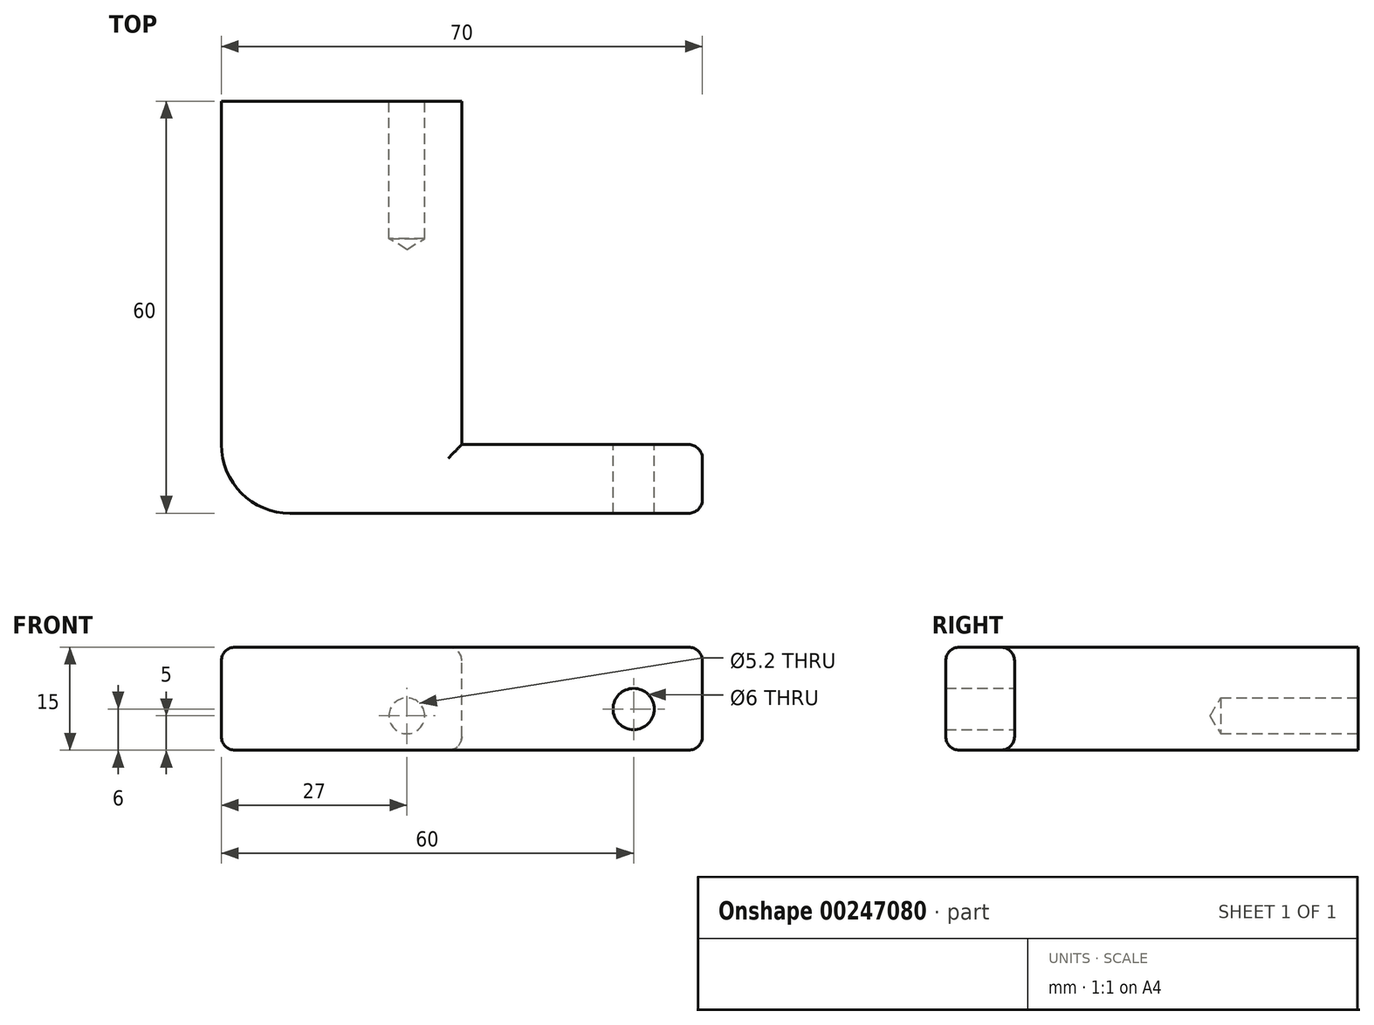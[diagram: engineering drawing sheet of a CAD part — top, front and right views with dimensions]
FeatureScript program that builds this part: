
annotation { "Feature Type Name" : "Feature", "Feature Type Description" : "" }
export const myFeature = defineFeature(function(context is Context, id is Id, definition is map)
    precondition{}
    {
        {
            var Q0;
            Q0=qCreatedBy(makeId("Front.planeOp"),FACE);
            var sketch = newSketch(context, id + "F0", { "sketchPlane" : qUnion([Q0])});
            skLineSegment(sketch, "E0.bottom", {"start": v(0, 0) * mm, "end": v(35, 0) * mm});
            skLineSegment(sketch, "E0.top", {"start": v(0, 15) * mm, "end": v(35, 15) * mm});
            skLineSegment(sketch, "E0.left", {"start": v(0, 0) * mm, "end": v(0, 15) * mm});
            skLineSegment(sketch, "E0.right", {"start": v(35, 0) * mm, "end": v(35, 15) * mm});
            skPoint(sketch, "E1", {"position": v(27, 5) * mm});
            skSolve(sketch);
        }
        {
            var Q0;
            Q0=makeQuery(id+"F0.imprint","IMPRINT",FACE,{"disambiguationData":[TD([[makeQuery(id+"F0.imprint","IMPRINT",EDGE,{"derivedFrom":sQuery(id+"F0.wireOp",EDGE,"E0.bottom")}),1.0]])]});
            extrude(context, id + "F1", {"entities" : qUnion([Q0]), "depth" : 50 * mm});
        }
        {
            var Q0;
            Q0=sQuery(id+"F0.wireOp",VERTEX,"E1");
            var Q1;
            Q1=makeQuery(id+"F1.opExtrude","SWEPT_BODY",BODY,{"disambiguationData":[OSD([sQuery(id+"F0.wireOp",EDGE,"E0.bottom"),sQuery(id+"F0.wireOp",EDGE,"E0.top"),sQuery(id+"F0.wireOp",EDGE,"E0.left"),sQuery(id+"F0.wireOp",EDGE,"E0.right")])]});
            hole(context, id + "F2", {"style" : HoleStyle.SIMPLE, "endStyle" : HoleEndStyle.BLIND, "oppositeDirection" : true, "holeDiameter" : 5.2 * mm, "holeDepth" : 20 * mm, "tappedDepth" : 12 * mm, "tapClearance" : 3, "locations" : qUnion([Q0]), "scope" : qUnion([Q1])});
        }
        {
            var Q0;
            Q0=makeQuery(id+"F1.opExtrude","CAP_FACE",FACE,{"disambiguationData":[OSD([sQuery(id+"F0.wireOp",EDGE,"E0.bottom"),sQuery(id+"F0.wireOp",EDGE,"E0.top"),sQuery(id+"F0.wireOp",EDGE,"E0.left"),sQuery(id+"F0.wireOp",EDGE,"E0.right")])],"isStart":false});
            var sketch = newSketch(context, id + "F3", { "sketchPlane" : qUnion([Q0])});
            skLineSegment(sketch, "E2.bottom", {"start": v(0, 0) * mm, "end": v(70, 0) * mm});
            skLineSegment(sketch, "E2.top", {"start": v(0, 15) * mm, "end": v(70, 15) * mm});
            skLineSegment(sketch, "E2.left", {"start": v(0, 0) * mm, "end": v(0, 15) * mm});
            skLineSegment(sketch, "E2.right", {"start": v(70, 0) * mm, "end": v(70, 15) * mm});
            skPoint(sketch, "E3", {"position": v(60, 6) * mm});
            skSolve(sketch);
        }
        {
            var Q0;
            Q0 = qSketchRegion(id + "F3", true);
            extrude(context, id + "F4", {"entities" : qUnion([Q0]), "operationType" : NewBodyOperationType.ADD, "depth" : 10 * mm});
        }
        {
            var Q0;
            Q0=sQuery(id+"F3.wireOp",VERTEX,"E3");
            var Q1;
            Q1=makeQuery(id+"F1.opExtrude","SWEPT_BODY",BODY,{"disambiguationData":[OSD([sQuery(id+"F0.wireOp",EDGE,"E0.bottom"),sQuery(id+"F0.wireOp",EDGE,"E0.top"),sQuery(id+"F0.wireOp",EDGE,"E0.left"),sQuery(id+"F0.wireOp",EDGE,"E0.right")])]});
            hole(context, id + "F5", {"style" : HoleStyle.SIMPLE, "endStyle" : HoleEndStyle.THROUGH, "oppositeDirection" : true, "holeDiameter" : 6 * mm, "tappedDepth" : 12 * mm, "tapClearance" : 3, "locations" : qUnion([Q0]), "scope" : qUnion([Q1])});
        }
        {
            var Q0;
            Q0=makeQuery(id+"F4.boolean.opBoolean","MERGE",EDGE,{"derivedFrom":[makeQuery(id+"F1.opExtrude","SWEPT_EDGE",EDGE,{"disambiguationData":[OSD([sQuery(id+"F0.wireOp",EDGE,"E0.bottom"),sQuery(id+"F0.wireOp",EDGE,"E0.left")])]}),makeQuery(id+"F4.opExtrude","SWEPT_EDGE",EDGE,{"disambiguationData":[OSD([sQuery(id+"F3.wireOp",EDGE,"E2.bottom"),sQuery(id+"F3.wireOp",EDGE,"E2.left")])]})]});
            var Q1;
            Q1=makeQuery(id+"F4.opExtrude","CAP_EDGE",EDGE,{"disambiguationData":[OSD([sQuery(id+"F3.wireOp",EDGE,"E2.bottom")])],"isStart":false});
            var Q2;
            Q2=makeQuery(id+"F4.opExtrude","SWEPT_EDGE",EDGE,{"disambiguationData":[OSD([sQuery(id+"F3.wireOp",EDGE,"E2.bottom"),sQuery(id+"F3.wireOp",EDGE,"E2.right")])]});
            var Q3;
            Q3=makeQuery(id+"F4.opExtrude","CAP_EDGE",EDGE,{"disambiguationData":[OSD([sQuery(id+"F3.wireOp",EDGE,"E2.bottom")])],"isStart":true});
            var Q4;
            Q4=makeQuery(id+"F1.opExtrude","SWEPT_EDGE",EDGE,{"disambiguationData":[OSD([sQuery(id+"F0.wireOp",EDGE,"E0.bottom"),sQuery(id+"F0.wireOp",EDGE,"E0.right")])]});
            var Q5;
            Q5=makeQuery(id+"F4.opExtrude","CAP_EDGE",EDGE,{"disambiguationData":[OSD([sQuery(id+"F3.wireOp",EDGE,"E2.right")])],"isStart":true});
            var Q6;
            Q6=makeQuery(id+"F4.opExtrude","CAP_EDGE",EDGE,{"disambiguationData":[OSD([sQuery(id+"F3.wireOp",EDGE,"E2.right")])],"isStart":false});
            var Q7;
            Q7=makeQuery(id+"F4.opExtrude","SWEPT_EDGE",EDGE,{"disambiguationData":[OSD([sQuery(id+"F3.wireOp",EDGE,"E2.top"),sQuery(id+"F3.wireOp",EDGE,"E2.right")])]});
            var Q8;
            Q8=makeQuery(id+"F4.opExtrude","CAP_EDGE",EDGE,{"disambiguationData":[OSD([sQuery(id+"F3.wireOp",EDGE,"E2.top")])],"isStart":true});
            var Q9;
            Q9=makeQuery(id+"F1.opExtrude","SWEPT_EDGE",EDGE,{"disambiguationData":[OSD([sQuery(id+"F0.wireOp",EDGE,"E0.top"),sQuery(id+"F0.wireOp",EDGE,"E0.right")])]});
            var Q10;
            Q10=makeQuery(id+"F4.opExtrude","CAP_EDGE",EDGE,{"disambiguationData":[OSD([sQuery(id+"F3.wireOp",EDGE,"E2.top")])],"isStart":false});
            var Q11;
            Q11=makeQuery(id+"F4.boolean.opBoolean","MERGE",EDGE,{"derivedFrom":[makeQuery(id+"F1.opExtrude","SWEPT_EDGE",EDGE,{"disambiguationData":[OSD([sQuery(id+"F0.wireOp",EDGE,"E0.top"),sQuery(id+"F0.wireOp",EDGE,"E0.left")])]}),makeQuery(id+"F4.opExtrude","SWEPT_EDGE",EDGE,{"disambiguationData":[OSD([sQuery(id+"F3.wireOp",EDGE,"E2.top"),sQuery(id+"F3.wireOp",EDGE,"E2.left")])]})]});
            fillet(context, id + "F6", {"entities" : qUnion([Q0, Q1, Q2, Q3, Q4, Q5, Q6, Q7, Q8, Q9, Q10, Q11]), "radius" : 2 * mm, "tangentPropagation" : true, "allowEdgeOverflow" : false});
        }
        {
            var Q0;
            Q0=makeQuery(id+"F1.opExtrude","CAP_EDGE",EDGE,{"disambiguationData":[OSD([sQuery(id+"F0.wireOp",EDGE,"E0.right")])],"isStart":false});
            var Q1;
            Q1=makeQuery(id+"F4.opExtrude","CAP_EDGE",EDGE,{"disambiguationData":[OSD([sQuery(id+"F3.wireOp",EDGE,"E2.left")])],"isStart":false});
            fillet(context, id + "F7", {"entities" : qUnion([Q0, Q1]), "radius" : 10 * mm, "tangentPropagation" : true, "allowEdgeOverflow" : false});
        }
    });
